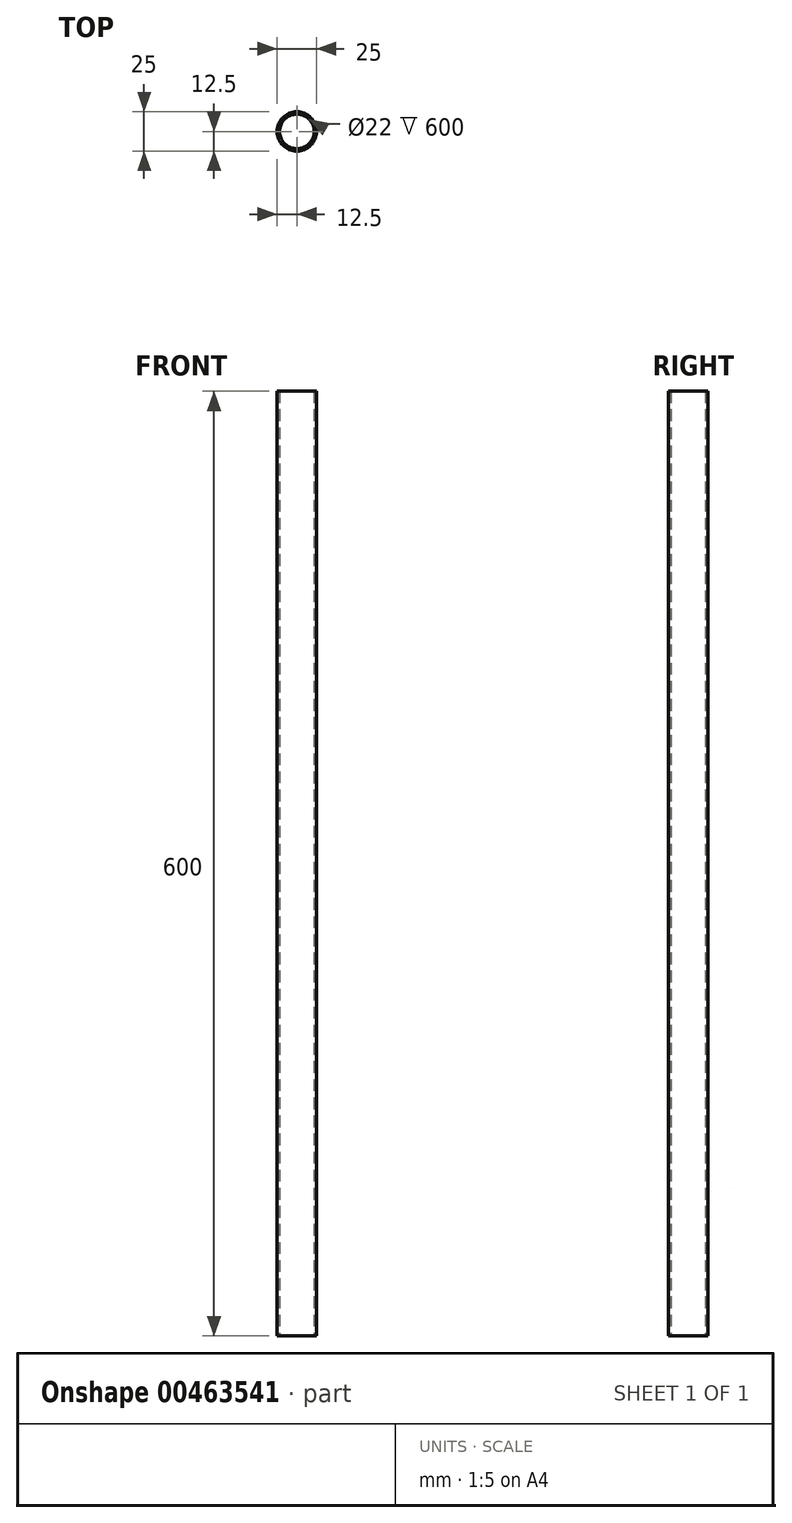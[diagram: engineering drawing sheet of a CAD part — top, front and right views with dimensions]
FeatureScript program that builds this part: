
annotation { "Feature Type Name" : "Feature", "Feature Type Description" : "" }
export const myFeature = defineFeature(function(context is Context, id is Id, definition is map)
    precondition{}
    {
        {
            var Q0;
            Q0=qCreatedBy(makeId("Top.planeOp"),FACE);
            var sketch = newSketch(context, id + "F0", { "sketchPlane" : qUnion([Q0])});
            skCircle(sketch, "E0", {"center": v(0, 0) * mm, "radius": 12.5 * mm});
            skCircle(sketch, "E1", {"center": v(0, 0) * mm, "radius": 11 * mm});
            skSolve(sketch);
        }
        {
            var Q0;
            Q0 = qSketchRegion(id + "F0", true);
            extrude(context, id + "F1", {"entities" : qUnion([Q0]), "depth" : 600 * mm, "offsetDistance" : 25 * mm});
        }
    });
